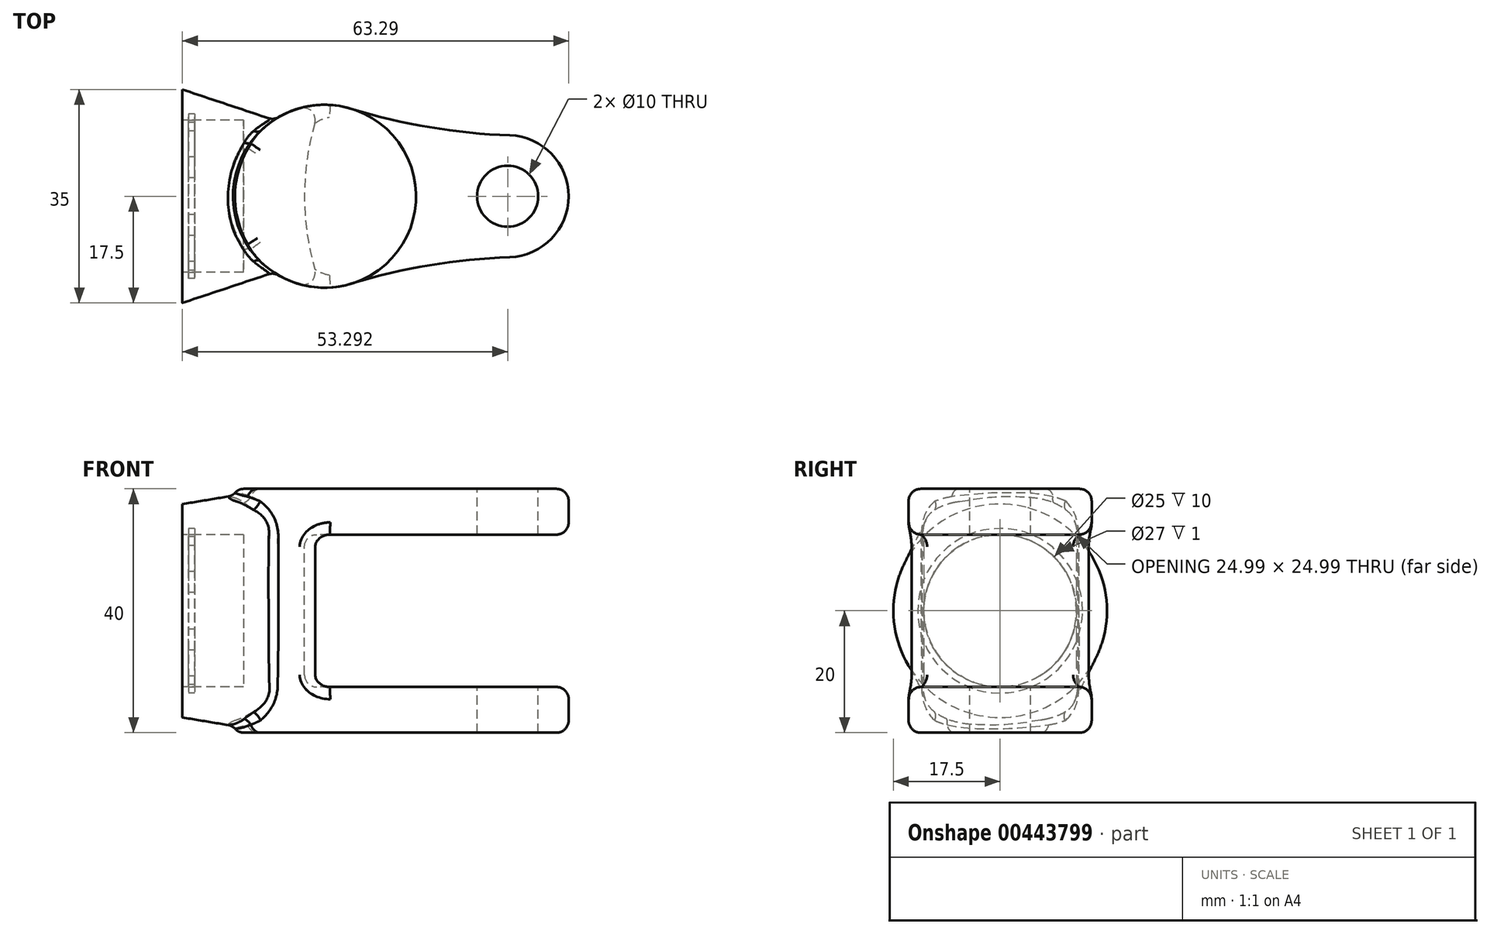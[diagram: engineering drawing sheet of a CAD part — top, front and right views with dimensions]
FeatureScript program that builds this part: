
annotation { "Feature Type Name" : "Feature", "Feature Type Description" : "" }
export const myFeature = defineFeature(function(context is Context, id is Id, definition is map)
    precondition{}
    {
        {
            var Q0;
            Q0=qCreatedBy(makeId("Right.planeOp"),FACE);
            var sketch = newSketch(context, id + "F0", { "sketchPlane" : qUnion([Q0])});
            skCircle(sketch, "E0", {"center": v(0, 0) * mm, "radius": 17.5 * mm});
            skSolve(sketch);
        }
        {
            var Q0;
            Q0=qCreatedBy(makeId("Right.planeOp"),FACE);
            cPlane(context, id + "F1", {"entities" : qUnion([Q0]), "cplaneType" : CPlaneType.OFFSET, "offset" : 15 * mm, "width" : 150 * mm, "height" : 150 * mm});
        }
        {
            var Q0;
            Q0=qCreatedBy(id+"F1.planeOp",FACE);
            var sketch = newSketch(context, id + "F2", { "sketchPlane" : qUnion([Q0])});
            skLineSegment(sketch, "E1.bottom", {"start": v(5, 20) * mm, "end": v(-5, 20) * mm});
            skLineSegment(sketch, "E1.top", {"start": v(5, -20) * mm, "end": v(-5, -20) * mm});
            skLineSegment(sketch, "E1.left", {"start": v(12.5, 12.5) * mm, "end": v(12.5, -12.5) * mm});
            skLineSegment(sketch, "E1.right", {"start": v(-12.5, 12.5) * mm, "end": v(-12.5, -12.5) * mm});
            skPoint(sketch, "E1.middle", {"position": v(0, 0) * mm});
            skPoint(sketch, "E2.visualSharp", {"position": v(-12.5, 20) * mm});
            skArc(sketch, "E2.filletArc", {"start": v(-5, 20) * mm, "mid": v(-10.3, 17.8) * mm, "end": v(-12.5, 12.5) * mm});
            skPoint(sketch, "E3.visualSharp", {"position": v(12.5, 20) * mm});
            skArc(sketch, "E3.filletArc", {"start": v(12.5, 12.5) * mm, "mid": v(10.3, 17.8) * mm, "end": v(5, 20) * mm});
            skPoint(sketch, "E4.visualSharp", {"position": v(12.5, -20) * mm});
            skArc(sketch, "E4.filletArc", {"start": v(5, -20) * mm, "mid": v(10.3, -17.8) * mm, "end": v(12.5, -12.5) * mm});
            skPoint(sketch, "E5.visualSharp", {"position": v(-12.5, -20) * mm});
            skArc(sketch, "E5.filletArc", {"start": v(-12.5, -12.5) * mm, "mid": v(-10.3, -17.8) * mm, "end": v(-5, -20) * mm});
            skSolve(sketch);
        }
        {
            var Q0;
            Q0=makeQuery(id+"F0.imprint","IMPRINT",FACE,{"disambiguationData":[TD([[makeQuery(id+"F0.imprint","IMPRINT",EDGE,{"derivedFrom":sQuery(id+"F0.wireOp",EDGE,"E0")}),1.0]])]});
            var Q1;
            Q1=makeQuery(id+"F2.imprint","IMPRINT",FACE,{"disambiguationData":[TD([[makeQuery(id+"F2.imprint","IMPRINT",EDGE,{"derivedFrom":sQuery(id+"F2.wireOp",EDGE,"E1.bottom")}),1.0]])]});
            loft(context, id + "F3", {"sheetProfilesArray" : [{ "sheetProfileEntities" : qUnion([Q0]) }, { "sheetProfileEntities" : qUnion([Q1]) }]});
        }
        {
            var Q0;
            Q0=qCreatedBy(makeId("Top.planeOp"),FACE);
            var sketch = newSketch(context, id + "F4", { "sketchPlane" : qUnion([Q0])});
            skArc(sketch, "E6", {"start": v(27.7, 14.34) * mm, "mid": v(8.3, 0) * mm, "end": v(27.7, -14.34) * mm});
            skArc(sketch, "E7", {"start": v(53.63, -10) * mm, "mid": v(63.3, 0) * mm, "end": v(53.63, 10) * mm});
            skArc(sketch, "E8", {"start": v(53.63, -10) * mm, "mid": v(40.52, -11.31) * mm, "end": v(27.7, -14.34) * mm});
            skArc(sketch, "E9", {"start": v(27.7, 14.34) * mm, "mid": v(40.52, 11.31) * mm, "end": v(53.63, 10) * mm});
            skSolve(sketch);
        }
        {
            var Q0;
            Q0 = qSketchRegion(id + "F4", true);
            extrude(context, id + "F5", {"entities" : qUnion([Q0]), "operationType" : NewBodyOperationType.ADD, "endBound" : BoundingType.SYMMETRIC, "depth" : 40 * mm});
        }
        {
            var Q0;
            Q0=qCreatedBy(makeId("Front.planeOp"),FACE);
            var sketch = newSketch(context, id + "F6", { "sketchPlane" : qUnion([Q0])});
            skLineSegment(sketch, "E10.bottom", {"start": v(63.3, -12.5) * mm, "end": v(20, -12.5) * mm});
            skLineSegment(sketch, "E10.top", {"start": v(63.3, 12.5) * mm, "end": v(20, 12.5) * mm});
            skLineSegment(sketch, "E10.left", {"start": v(63.3, -12.5) * mm, "end": v(63.3, 12.5) * mm});
            skLineSegment(sketch, "E10.right", {"start": v(20, -12.5) * mm, "end": v(20, 12.5) * mm});
            skPoint(sketch, "E10.middle", {"position": v(41.65, 0) * mm});
            skSolve(sketch);
        }
        {
            var Q0;
            Q0 = qSketchRegion(id + "F6", true);
            var Q1;
            Q1=sQuery(id+"F6.wireOp",EDGE,"E10.left");
            revolve(context, id + "F7", {"operationType" : NewBodyOperationType.REMOVE, "entities" : qUnion([Q0]), "axis" : qUnion([Q1]), "revolveType" : RevolveType.FULL, "oppositeDirection" : true});
        }
        {
            var Q0;
            Q0=makeQuery(id+"F3.opLoft","CAP_FACE",FACE,{"disambiguationData":[OSD([makeQuery(id+"F0.imprint","IMPRINT",FACE,{"disambiguationData":[TD([[makeQuery(id+"F0.imprint","IMPRINT",EDGE,{"derivedFrom":sQuery(id+"F0.wireOp",EDGE,"E0")}),1.0]])]})])],"isStart":true});
            var sketch = newSketch(context, id + "F8", { "sketchPlane" : qUnion([Q0])});
            skCircle(sketch, "E11", {"center": v(0, 0) * mm, "radius": 12.5 * mm});
            skSolve(sketch);
        }
        {
            var Q0;
            Q0 = qSketchRegion(id + "F8", true);
            extrude(context, id + "F9", {"entities" : qUnion([Q0]), "operationType" : NewBodyOperationType.REMOVE, "oppositeDirection" : true, "depth" : 10 * mm});
        }
        {
            var Q0;
            Q0=makeQuery(id+"F3.opLoft","CAP_FACE",FACE,{"disambiguationData":[OSD([makeQuery(id+"F0.imprint","IMPRINT",FACE,{"disambiguationData":[TD([[makeQuery(id+"F0.imprint","IMPRINT",EDGE,{"derivedFrom":sQuery(id+"F0.wireOp",EDGE,"E0")}),1.0]])]})])],"isStart":true});
            cPlane(context, id + "F10", {"entities" : qUnion([Q0]), "cplaneType" : CPlaneType.OFFSET, "offset" : 1 * mm, "oppositeDirection" : true, "width" : 150 * mm, "height" : 150 * mm});
        }
        {
            var Q0;
            Q0=qCreatedBy(id+"F10.planeOp",FACE);
            var sketch = newSketch(context, id + "F11", { "sketchPlane" : qUnion([Q0])});
            skCircle(sketch, "E12.0", {"center": v(0, 0) * mm, "radius": 13.5 * mm});
            skFitSpline(sketch, "E13.0", {"points": [v(12.13, 3.03) * mm, v(12.03, 3.43) * mm, v(11.8, 4.21) * mm, v(11.32, 5.35) * mm, v(10.84, 6.25) * mm, v(10.4, 6.94) * mm, v(10.05, 7.45) * mm, v(9.67, 7.93) * mm, v(9.27, 8.4) * mm, v(8.85, 8.84) * mm, v(8.25, 9.4) * mm, v(7.46, 10.05) * mm, v(6.78, 10.5) * mm, v(6.43, 10.72) * mm]});
            skFitSpline(sketch, "E13.1", {"points": [v(10.72, -6.43) * mm, v(10.93, -6.08) * mm, v(11.31, -5.36) * mm, v(11.79, -4.22) * mm, v(12.08, -3.24) * mm, v(12.26, -2.45) * mm, v(12.37, -1.84) * mm, v(12.44, -1.23) * mm, v(12.49, -0.62) * mm, v(12.5, 0) * mm, v(12.49, 0.81) * mm, v(12.39, 1.83) * mm, v(12.23, 2.63) * mm, v(12.13, 3.03) * mm]});
            skFitSpline(sketch, "E13.2", {"points": [v(6.43, 10.72) * mm, v(6.08, 10.93) * mm, v(5.36, 11.31) * mm, v(4.22, 11.79) * mm, v(3.24, 12.08) * mm, v(2.45, 12.26) * mm, v(1.84, 12.37) * mm, v(1.23, 12.44) * mm, v(0.62, 12.49) * mm, v(0, 12.5) * mm, v(-0.81, 12.49) * mm, v(-1.83, 12.39) * mm, v(-2.63, 12.23) * mm, v(-3.03, 12.13) * mm]});
            skFitSpline(sketch, "E13.3", {"points": [v(3.03, -12.13) * mm, v(3.43, -12.03) * mm, v(4.21, -11.8) * mm, v(5.35, -11.32) * mm, v(6.25, -10.84) * mm, v(6.94, -10.4) * mm, v(7.45, -10.05) * mm, v(7.93, -9.67) * mm, v(8.4, -9.27) * mm, v(8.84, -8.85) * mm, v(9.4, -8.25) * mm, v(10.05, -7.46) * mm, v(10.5, -6.78) * mm, v(10.72, -6.43) * mm]});
            skFitSpline(sketch, "E13.4", {"points": [v(-3.03, 12.13) * mm, v(-3.43, 12.03) * mm, v(-4.21, 11.8) * mm, v(-5.35, 11.32) * mm, v(-6.25, 10.84) * mm, v(-6.94, 10.4) * mm, v(-7.45, 10.05) * mm, v(-7.93, 9.67) * mm, v(-8.4, 9.27) * mm, v(-8.84, 8.85) * mm, v(-9.4, 8.25) * mm, v(-10.05, 7.46) * mm, v(-10.5, 6.78) * mm, v(-10.72, 6.43) * mm]});
            skFitSpline(sketch, "E13.5", {"points": [v(-10.72, 6.43) * mm, v(-10.93, 6.08) * mm, v(-11.31, 5.36) * mm, v(-11.79, 4.22) * mm, v(-12.08, 3.24) * mm, v(-12.26, 2.45) * mm, v(-12.37, 1.84) * mm, v(-12.44, 1.23) * mm, v(-12.49, 0.62) * mm, v(-12.5, 0) * mm, v(-12.49, -0.81) * mm, v(-12.39, -1.83) * mm, v(-12.23, -2.63) * mm, v(-12.13, -3.03) * mm]});
            skFitSpline(sketch, "E13.6", {"points": [v(-12.13, -3.03) * mm, v(-12.03, -3.43) * mm, v(-11.8, -4.21) * mm, v(-11.32, -5.35) * mm, v(-10.84, -6.25) * mm, v(-10.4, -6.94) * mm, v(-10.05, -7.45) * mm, v(-9.67, -7.93) * mm, v(-9.27, -8.4) * mm, v(-8.85, -8.84) * mm, v(-8.25, -9.4) * mm, v(-7.46, -10.05) * mm, v(-6.78, -10.5) * mm, v(-6.43, -10.72) * mm]});
            skFitSpline(sketch, "E13.7", {"points": [v(-6.43, -10.72) * mm, v(-6.08, -10.93) * mm, v(-5.36, -11.31) * mm, v(-4.22, -11.79) * mm, v(-3.24, -12.08) * mm, v(-2.45, -12.26) * mm, v(-1.84, -12.37) * mm, v(-1.23, -12.44) * mm, v(-0.62, -12.49) * mm, v(0, -12.5) * mm, v(0.81, -12.49) * mm, v(1.83, -12.39) * mm, v(2.63, -12.23) * mm, v(3.03, -12.13) * mm]});
            skSolve(sketch);
        }
        {
            var Q0;
            Q0 = qSketchRegion(id + "F11", true);
            extrude(context, id + "F12", {"entities" : qUnion([Q0]), "operationType" : NewBodyOperationType.REMOVE, "oppositeDirection" : true, "depth" : 1 * mm});
        }
        {
            var Q0;
            Q0=makeQuery(id+"F5.opExtrude","CAP_FACE",FACE,{"disambiguationData":[OSD([sQuery(id+"F4.wireOp",EDGE,"E6"),sQuery(id+"F4.wireOp",EDGE,"E7"),sQuery(id+"F4.wireOp",EDGE,"E8"),sQuery(id+"F4.wireOp",EDGE,"E9")])],"isStart":false});
            var sketch = newSketch(context, id + "F13", { "sketchPlane" : qUnion([Q0])});
            skCircle(sketch, "E14", {"center": v(53.3, 0) * mm, "radius": 5 * mm});
            skSolve(sketch);
        }
        {
            var Q0;
            Q0 = qSketchRegion(id + "F13", true);
            extrude(context, id + "F14", {"entities" : qUnion([Q0]), "operationType" : NewBodyOperationType.REMOVE, "endBound" : BoundingType.THROUGH_ALL, "oppositeDirection" : true, "depth" : 25 * mm});
        }
        {
            var Q0;
            Q0=makeQuery(id+"F7.boolean.opBoolean","COPY",EDGE,{"derivedFrom":makeQuery(id+"F7.opRevolve","SWEPT_EDGE",EDGE,{"disambiguationData":[OSD([sQuery(id+"F6.wireOp",EDGE,"E10.bottom"),sQuery(id+"F6.wireOp",EDGE,"E10.right")])]})});
            var Q1;
            Q1=makeQuery(id+"F7.boolean.opBoolean","COPY",EDGE,{"derivedFrom":makeQuery(id+"F7.opRevolve","SWEPT_EDGE",EDGE,{"disambiguationData":[OSD([sQuery(id+"F6.wireOp",EDGE,"E10.top"),sQuery(id+"F6.wireOp",EDGE,"E10.right")])]})});
            fillet(context, id + "F15", {"entities" : qUnion([Q0, Q1]), "radius" : 2 * mm, "tangentPropagation" : true, "allowEdgeOverflow" : false});
        }
        {
            var Q0;
            {var subQ2=sQuery(id+"F4.wireOp",EDGE,"E7");Q0=makeQuery(id+"F7.boolean.opBoolean","SPLIT",FACE,{"disambiguationData":[TD([makeQuery(id+"F7.opRevolve","SWEPT_FACE",FACE,{"disambiguationData":[OSD([sQuery(id+"F6.wireOp",EDGE,"E10.bottom")])]})])],"derivedFrom":makeQuery(id+"F5.opExtrude","SWEPT_FACE",FACE,{"disambiguationData":[OSD([subQ2])]})});}
            var Q1;
            {var subQ1=sQuery(id+"F4.wireOp",EDGE,"E9");Q1=makeQuery(id+"F7.boolean.opBoolean","SPLIT",FACE,{"disambiguationData":[TD([makeQuery(id+"F7.opRevolve","SWEPT_FACE",FACE,{"disambiguationData":[OSD([sQuery(id+"F6.wireOp",EDGE,"E10.bottom")])]})])],"derivedFrom":makeQuery(id+"F5.opExtrude","SWEPT_FACE",FACE,{"disambiguationData":[OSD([subQ1])]})});}
            var Q2;
            {var subQ1=sQuery(id+"F4.wireOp",EDGE,"E8");Q2=makeQuery(id+"F7.boolean.opBoolean","SPLIT",FACE,{"disambiguationData":[TD([makeQuery(id+"F7.opRevolve","SWEPT_FACE",FACE,{"disambiguationData":[OSD([sQuery(id+"F6.wireOp",EDGE,"E10.bottom")])]})])],"derivedFrom":makeQuery(id+"F5.opExtrude","SWEPT_FACE",FACE,{"disambiguationData":[OSD([subQ1])]})});}
            var Q3;
            {var subQ1=sQuery(id+"F4.wireOp",EDGE,"E9");Q3=makeQuery(id+"F7.boolean.opBoolean","SPLIT",FACE,{"disambiguationData":[TD([makeQuery(id+"F7.opRevolve","SWEPT_FACE",FACE,{"disambiguationData":[OSD([sQuery(id+"F6.wireOp",EDGE,"E10.top")])]})])],"derivedFrom":makeQuery(id+"F5.opExtrude","SWEPT_FACE",FACE,{"disambiguationData":[OSD([subQ1])]})});}
            var Q4;
            {var subQ2=sQuery(id+"F4.wireOp",EDGE,"E7");Q4=makeQuery(id+"F7.boolean.opBoolean","SPLIT",FACE,{"disambiguationData":[TD([makeQuery(id+"F7.opRevolve","SWEPT_FACE",FACE,{"disambiguationData":[OSD([sQuery(id+"F6.wireOp",EDGE,"E10.top")])]})])],"derivedFrom":makeQuery(id+"F5.opExtrude","SWEPT_FACE",FACE,{"disambiguationData":[OSD([subQ2])]})});}
            var Q5;
            {var subQ1=sQuery(id+"F4.wireOp",EDGE,"E8");Q5=makeQuery(id+"F7.boolean.opBoolean","SPLIT",FACE,{"disambiguationData":[TD([makeQuery(id+"F7.opRevolve","SWEPT_FACE",FACE,{"disambiguationData":[OSD([sQuery(id+"F6.wireOp",EDGE,"E10.top")])]})])],"derivedFrom":makeQuery(id+"F5.opExtrude","SWEPT_FACE",FACE,{"disambiguationData":[OSD([subQ1])]})});}
            fillet(context, id + "F16", {"entities" : qUnion([Q0, Q1, Q2, Q3, Q4, Q5]), "radius" : 2 * mm, "tangentPropagation" : true, "allowEdgeOverflow" : false});
        }
        {
            var Q0;
            Q0=makeQuery(id+"F3.opLoft","MID_CAP_EDGE",EDGE,{"disambiguationData":[OSD([sQuery(id+"F2.wireOp",EDGE,"E1.right"),sQuery(id+"F2.wireOp",EDGE,"E2.filletArc"),sQuery(id+"F2.wireOp",EDGE,"E5.filletArc")])],"capPos":1.0});
            var Q1;
            Q1=makeQuery(id+"F5.boolean.opBoolean","INTERSECT",EDGE,{"disambiguationData":[OD(0.0)],"derivedFrom":[makeQuery(id+"F3.opLoft","SWEPT_FACE",FACE,{"disambiguationData":[OSD([sQuery(id+"F0.wireOp",EDGE,"E0"),sQuery(id+"F2.wireOp",EDGE,"E1.bottom"),sQuery(id+"F2.wireOp",EDGE,"E2.filletArc"),sQuery(id+"F2.wireOp",EDGE,"E3.filletArc")])]}),makeQuery(id+"F5.opExtrude","SWEPT_FACE",FACE,{"disambiguationData":[OSD([sQuery(id+"F4.wireOp",EDGE,"E6")])]})]});
            var Q2;
            Q2=makeQuery(id+"F16.opFillet","BLEND_EDGE",EDGE,{"blendedFrom":[makeQuery(id+"F5.opExtrude","CAP_EDGE",EDGE,{"disambiguationData":[OSD([sQuery(id+"F4.wireOp",EDGE,"E6")])],"isStart":false}),makeQuery(id+"F3.opLoft","SWEPT_FACE",FACE,{"disambiguationData":[OSD([sQuery(id+"F0.wireOp",EDGE,"E0"),sQuery(id+"F2.wireOp",EDGE,"E1.bottom"),sQuery(id+"F2.wireOp",EDGE,"E2.filletArc"),sQuery(id+"F2.wireOp",EDGE,"E3.filletArc")])]})],"blendedInto":[makeQuery(id+"F3.opLoft","SWEPT_FACE",FACE,{"disambiguationData":[OSD([sQuery(id+"F0.wireOp",EDGE,"E0"),sQuery(id+"F2.wireOp",EDGE,"E1.bottom"),sQuery(id+"F2.wireOp",EDGE,"E2.filletArc"),sQuery(id+"F2.wireOp",EDGE,"E3.filletArc")])]})]});
            var Q3;
            Q3=makeQuery(id+"F5.boolean.opBoolean","INTERSECT",EDGE,{"disambiguationData":[OD(1.0)],"derivedFrom":[makeQuery(id+"F3.opLoft","SWEPT_FACE",FACE,{"disambiguationData":[OSD([sQuery(id+"F0.wireOp",EDGE,"E0"),sQuery(id+"F2.wireOp",EDGE,"E1.bottom"),sQuery(id+"F2.wireOp",EDGE,"E2.filletArc"),sQuery(id+"F2.wireOp",EDGE,"E3.filletArc")])]}),makeQuery(id+"F5.opExtrude","SWEPT_FACE",FACE,{"disambiguationData":[OSD([sQuery(id+"F4.wireOp",EDGE,"E6")])]})]});
            var Q4;
            Q4=makeQuery(id+"F3.opLoft","MID_CAP_EDGE",EDGE,{"disambiguationData":[OSD([sQuery(id+"F2.wireOp",EDGE,"E1.left"),sQuery(id+"F2.wireOp",EDGE,"E3.filletArc"),sQuery(id+"F2.wireOp",EDGE,"E4.filletArc")])],"capPos":1.0});
            var Q5;
            Q5=makeQuery(id+"F16.opFillet","BLEND_EDGE",EDGE,{"blendedFrom":[makeQuery(id+"F5.opExtrude","CAP_EDGE",EDGE,{"disambiguationData":[OSD([sQuery(id+"F4.wireOp",EDGE,"E6")])],"isStart":true}),makeQuery(id+"F3.opLoft","SWEPT_FACE",FACE,{"disambiguationData":[OSD([sQuery(id+"F0.wireOp",EDGE,"E0"),sQuery(id+"F2.wireOp",EDGE,"E1.bottom"),sQuery(id+"F2.wireOp",EDGE,"E2.filletArc"),sQuery(id+"F2.wireOp",EDGE,"E3.filletArc")])]})],"blendedInto":[makeQuery(id+"F3.opLoft","SWEPT_FACE",FACE,{"disambiguationData":[OSD([sQuery(id+"F0.wireOp",EDGE,"E0"),sQuery(id+"F2.wireOp",EDGE,"E1.bottom"),sQuery(id+"F2.wireOp",EDGE,"E2.filletArc"),sQuery(id+"F2.wireOp",EDGE,"E3.filletArc")])]})]});
            fillet(context, id + "F17", {"entities" : qUnion([Q0, Q1, Q2, Q3, Q4, Q5]), "radius" : 2 * mm, "tangentPropagation" : true, "allowEdgeOverflow" : false});
        }
    });
